# Revit family: LRTS
name_source: partatom
category: Lighting Fixtures
units: mm (PartAtom-declared; Revit-internal decimal feet)

## family parameters
Always vertical = Yes
Cut with Voids When Loaded = No
Host = Ceiling
Light Source = Yes
OmniClass Number = 23.80.70.11.14.17
OmniClass Title = Direct/Indirect
Part Type = Normal
Room Calculation Point = No
Round Connector Dimension = Use Diameter
Shared = No

## types (12) — shared parameters
Assembly Code = D5020200
Color Filter = 16777215
Description = Architectural Recessed Troffer Type S
Dimming Lamp Color Temperature Shift = <None>
Emit Shape Visible in Rendering = No
Emit from Rectangle Height = 0' - 0 1/8"
Housing Finish = Metal - Viscor - White
Lamp = LED
Lens Depth = 0' - 0 1/8"
Lens Finish = Acrylic - Viscor - Frosted White
Manufacturer = VISIONEERING by VISCOR
Model = LRTS
Tilt Angle = 90.00°
URL = https://viscor.com
Voltage = 120 V

## per-type parameters (varying)
| type | Apparent Load | Emit from Rectangle Length | Emit from Rectangle Width | Lamp Wattage | Length | Photometric Web File | Width |
| LRTS2X4-LED840K030LUNV | 35 VA | 3' - 11 3/4" | 1' - 11 7/16" | 35 VA | 3' - 11 3/4" | LRTS2X4-LED840K030LUNV.ies | 1' - 11 7/16" |
| LRTS2X4-LED840K050LUNV | 59 VA | 3' - 11 3/4" | 1' - 11 7/16" | 59 VA | 3' - 11 3/4" | LRTS2X4-LED840K050LUNV.ies | 1' - 11 7/16" |
| LRTS2X2-LED840K027LUNV | 35 VA | 1' - 11 3/4" | 1' - 11 7/16" | 35 VA | 1' - 11 3/4" | LRTS2X2-LED840K027LUNV.ies | 1' - 11 7/16" |
| LRTS2X2-LED840K019LUNV | 25 VA | 1' - 11 3/4" | 1' - 11 7/16" | 25 VA | 1' - 11 3/4" | LRTS2X2-LED840K019LUNV.ies | 1' - 11 7/16" |
| LRTS2X2-LED840K036LUNV | 47 VA | 1' - 11 3/4" | 1' - 11 7/16" | 47 VA | 1' - 11 3/4" | LRTS2X2-LED840K036LUNV.ies | 1' - 11 7/16" |
| LRTS2X2-LED840K043LUNV | 58 VA | 1' - 11 3/4" | 1' - 11 7/16" | 58 VA | 1' - 11 3/4" | LRTS2X2-LED840K043LUNV.ies | 1' - 11 7/16" |
| LRTS2X4-LED840K040LUNV | 47 VA | 3' - 11 3/4" | 1' - 11 7/16" | 47 VA | 3' - 11 3/4" | LRTS2X4-LED840K040LUNV.ies | 1' - 11 7/16" |
| LRTS2X4-LED840K065LUNV | 77 VA | 3' - 11 3/4" | 1' - 11 7/16" | 77 VA | 3' - 11 3/4" | LRTS2X4-LED840K065LUNV.ies | 1' - 11 7/16" |
| LRTS1X4-LED840K030LUNV | 34 VA | 3' - 11 3/4" | 0' - 11 13/16" | 34 VA | 3' - 11 3/4" | LRTS1X4-LED840K030LUNV.ies | 0' - 11 13/16" |
| LRTS1X4-LED840K040LUNV | 46 VA | 3' - 11 3/4" | 0' - 11 13/16" | 46 VA | 3' - 11 3/4" | LRTS1X4-LED840K040LUNV.ies | 0' - 11 13/16" |
| LRTS1X4-LED840K050LUNV | 58 VA | 3' - 11 3/4" | 0' - 11 13/16" | 58 VA | 3' - 11 3/4" | LRTS1X4-LED840K050LUNV.ies | 0' - 11 13/16" |
| LRTS1X4-LED840K065LUNV | 78 VA | 3' - 11 3/4" | 0' - 11 13/16" | 78 VA | 3' - 11 3/4" | LRTS1X4-LED840K065LUNV.ies | 0' - 11 13/16" |

## geometry (parser evidence)
native form markers: Sweep x3
no freeform markers — native parametric forms only
